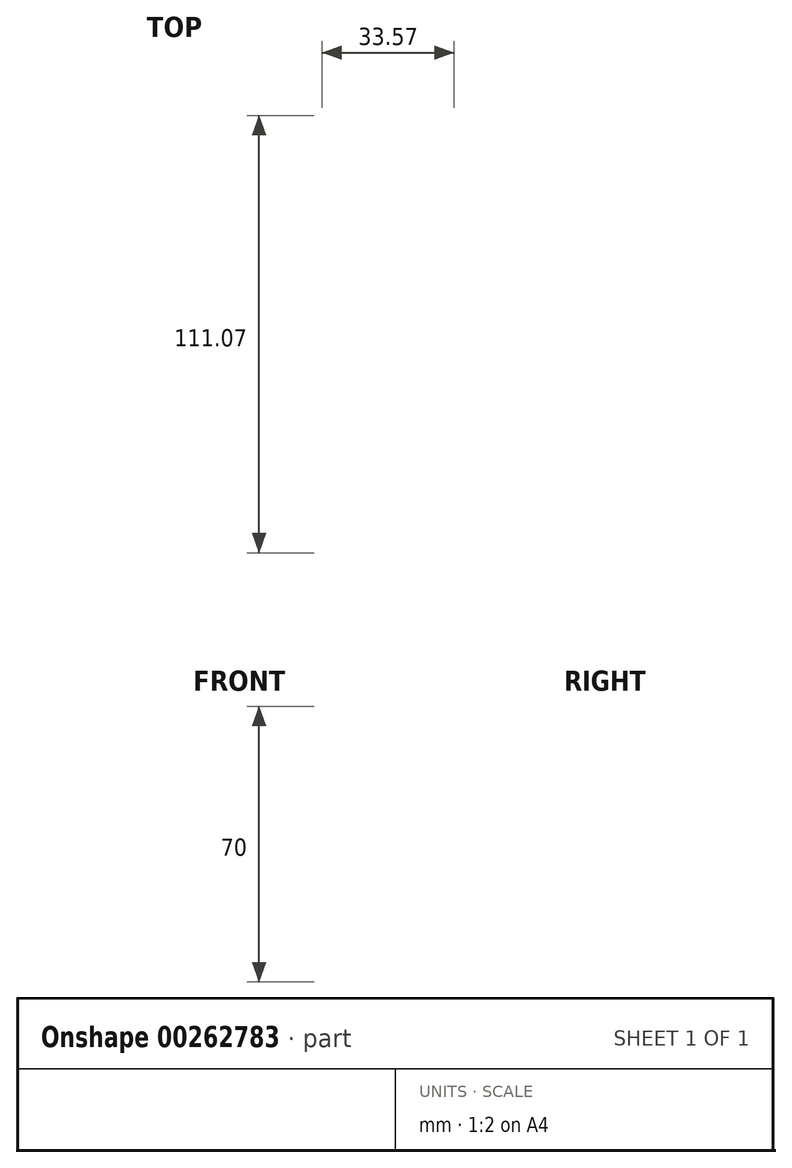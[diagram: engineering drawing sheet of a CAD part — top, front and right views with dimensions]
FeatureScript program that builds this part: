
annotation { "Feature Type Name" : "Feature", "Feature Type Description" : "" }
export const myFeature = defineFeature(function(context is Context, id is Id, definition is map)
    precondition{}
    {
        {
            var Q0;
            Q0=qCreatedBy(makeId("Top.planeOp"),FACE);
            cPlane(context, id + "F0", {"entities" : qUnion([Q0]), "cplaneType" : CPlaneType.OFFSET, "offset" : 50 * mm, "width" : 150 * mm, "height" : 150 * mm});
        }
        {
            var Q0;
            Q0=qCreatedBy(makeId("Top.planeOp"),FACE);
            cPlane(context, id + "F1", {"entities" : qUnion([Q0]), "cplaneType" : CPlaneType.OFFSET, "offset" : 25 * mm, "width" : 150 * mm, "height" : 150 * mm});
        }
        {
            var Q0;
            Q0=qCreatedBy(id+"F0.planeOp",FACE);
            var sketch = newSketch(context, id + "F2", { "sketchPlane" : qUnion([Q0])});
            skArc(sketch, "E0", {"start": v(0, 73.62) * mm, "mid": v(-9.31, 41.4) * mm, "end": v(-17.44, 8.87) * mm});
            skArc(sketch, "E1", {"start": v(16.1, 8.87) * mm, "mid": v(9.52, 41.6) * mm, "end": v(0, 73.62) * mm});
            skArc(sketch, "E2", {"start": v(-17.44, 8.87) * mm, "mid": v(-15.36, -14.5) * mm, "end": v(-10.54, -37.45) * mm});
            skArc(sketch, "E3", {"start": v(10.03, -37.45) * mm, "mid": v(14.82, -14.52) * mm, "end": v(16.1, 8.87) * mm});
            skLineSegment(sketch, "E4", {"start": v(-10.54, -37.45) * mm, "end": v(10.03, -37.45) * mm});
            skSolve(sketch);
        }
        {
            var Q0;
            Q0=qCreatedBy(id+"F1.planeOp",FACE);
            var sketch = newSketch(context, id + "F3", { "sketchPlane" : qUnion([Q0])});
            skEllipse(sketch, "E5", {"center": v(0, 18.54) * mm, "majorRadius": 54.83 * mm, "minorRadius": 4.29 * mm, "majorAxis": v(0, -1)});
            skSolve(sketch);
        }
        {
            var Q0;
            Q0=makeQuery(id+"F2.imprint","IMPRINT",FACE,{"disambiguationData":[TD([[makeQuery(id+"F2.imprint","IMPRINT",EDGE,{"derivedFrom":sQuery(id+"F2.wireOp",EDGE,"E0")}),1.0]])]});
            var Q1;
            Q1=makeQuery(id+"F3.imprint","IMPRINT",FACE,{"disambiguationData":[TD([[makeQuery(id+"F3.imprint","IMPRINT",EDGE,{"derivedFrom":sQuery(id+"F3.wireOp",EDGE,"E5")}),1.0]])]});
            loft(context, id + "F4", {"sheetProfilesArray" : [{ "sheetProfileEntities" : qUnion([Q0]) }, { "sheetProfileEntities" : qUnion([Q1]) }]});
        }
        {
            var Q0;
            Q0=makeQuery(id+"F4.opLoft","CAP_FACE",FACE,{"disambiguationData":[OSD([makeQuery(id+"F2.imprint","IMPRINT",FACE,{"disambiguationData":[TD([[makeQuery(id+"F2.imprint","IMPRINT",EDGE,{"derivedFrom":sQuery(id+"F2.wireOp",EDGE,"E0")}),1.0]])]})])],"isStart":true});
            shell(context, id + "F5", {"entities" : qUnion([Q0]), "thickness" : 2.5 * mm});
        }
        {
            var Q0;
            Q0=qCreatedBy(id+"F1.planeOp",FACE);
            var sketch = newSketch(context, id + "F6", { "sketchPlane" : qUnion([Q0])});
            skCircle(sketch, "E6", {"center": v(0, 12.15) * mm, "radius": 2.06 * mm});
            skSolve(sketch);
        }
        {
            var Q0;
            Q0 = qSketchRegion(id + "F6", true);
            extrude(context, id + "F7", {"entities" : qUnion([Q0]), "operationType" : NewBodyOperationType.ADD, "depth" : 70 * mm});
        }
    });
